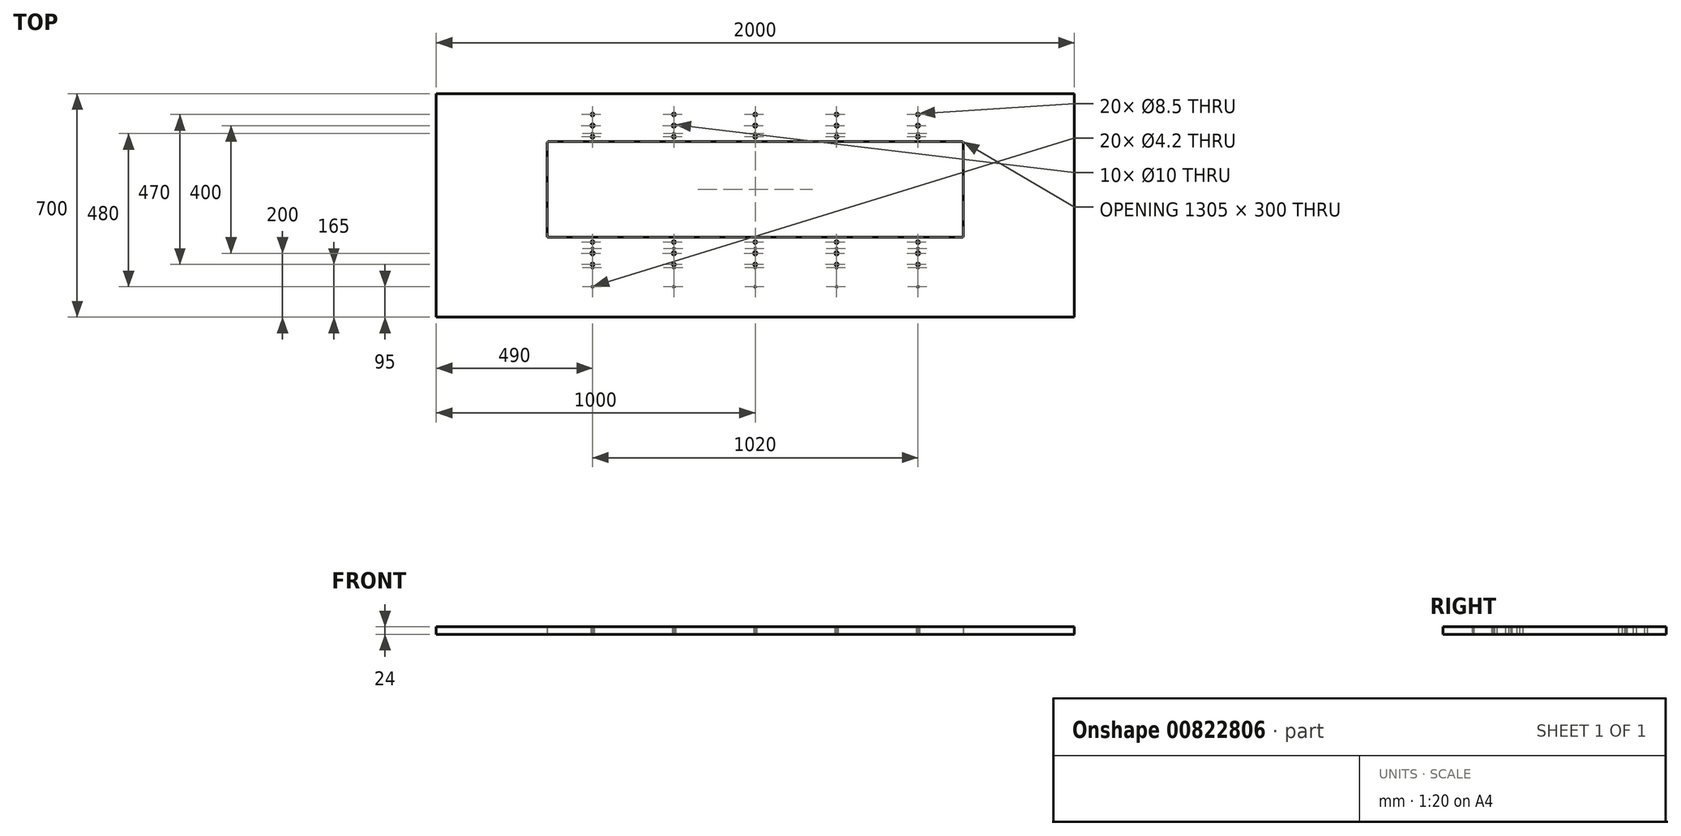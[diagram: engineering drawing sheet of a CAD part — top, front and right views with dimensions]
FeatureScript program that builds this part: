
annotation { "Feature Type Name" : "Feature", "Feature Type Description" : "" }
export const myFeature = defineFeature(function(context is Context, id is Id, definition is map)
    precondition{}
    {
        {
            var Q0;
            Q0=qCreatedBy(makeId("Top.planeOp"),FACE);
            var sketch = newSketch(context, id + "F0", { "sketchPlane" : qUnion([Q0])});
            skLineSegment(sketch, "E0.bottom", {"start": v(-652.5, -150) * mm, "end": v(652.5, -150) * mm});
            skLineSegment(sketch, "E0.top", {"start": v(-652.5, 150) * mm, "end": v(652.5, 150) * mm});
            skLineSegment(sketch, "E0.left", {"start": v(-652.5, -150) * mm, "end": v(-652.5, 150) * mm});
            skLineSegment(sketch, "E0.right", {"start": v(652.5, -150) * mm, "end": v(652.5, 150) * mm});
            skPoint(sketch, "E0.middle", {"position": v(0, 0) * mm});
            skLineSegment(sketch, "E1.top", {"start": v(-1000, 300) * mm, "end": v(1000, 300) * mm});
            skLineSegment(sketch, "E2.bottom", {"start": v(-510, 165) * mm, "end": v(510, 165) * mm, "construction": true});
            skLineSegment(sketch, "E2.top", {"start": v(-510, -165) * mm, "end": v(510, -165) * mm, "construction": true});
            skLineSegment(sketch, "E2.left", {"start": v(-510, 165) * mm, "end": v(-510, -165) * mm, "construction": true});
            skLineSegment(sketch, "E2.right", {"start": v(510, 165) * mm, "end": v(510, -165) * mm, "construction": true});
            skLineSegment(sketch, "E3", {"start": v(-255, 314.2) * mm, "end": v(-255, -334.02) * mm, "construction": true});
            skLineSegment(sketch, "E4", {"start": v(0, 0) * mm, "end": v(0, 282.14) * mm, "construction": true});
            skLineSegment(sketch, "E5", {"start": v(0, 0) * mm, "end": v(-747.83, 0) * mm, "construction": true});
            skLineSegment(sketch, "E6.0", {"start": v(-510, 235) * mm, "end": v(510, 235) * mm, "construction": true});
            skLineSegment(sketch, "E7.0", {"start": v(-510, -235) * mm, "end": v(510, -235) * mm, "construction": true});
            skLineSegment(sketch, "E8.0", {"start": v(-510, 200) * mm, "end": v(510, 200) * mm, "construction": true});
            skCircle(sketch, "E9", {"center": v(-510, 165) * mm, "radius": 4.25 * mm});
            skCircle(sketch, "E10", {"center": v(-510, 200) * mm, "radius": 5 * mm});
            skCircle(sketch, "E11", {"center": v(-510, 235) * mm, "radius": 4.25 * mm});
            skCircle(sketch, "E12", {"center": v(-255, 165) * mm, "radius": 4.25 * mm});
            skCircle(sketch, "E13", {"center": v(-255, 200) * mm, "radius": 5 * mm});
            skCircle(sketch, "E14", {"center": v(-255, 235) * mm, "radius": 4.25 * mm});
            skCircle(sketch, "E15", {"center": v(0, 165) * mm, "radius": 4.25 * mm});
            skCircle(sketch, "E16", {"center": v(0, 200) * mm, "radius": 5 * mm});
            skCircle(sketch, "E17", {"center": v(0, 235) * mm, "radius": 4.25 * mm});
            skCircle(sketch, "E18.MirrorC", {"center": v(510, 165) * mm, "radius": 4.25 * mm});
            skCircle(sketch, "E19.MirrorC", {"center": v(510, 200) * mm, "radius": 5 * mm});
            skCircle(sketch, "E20.MirrorC", {"center": v(510, 235) * mm, "radius": 4.25 * mm});
            skCircle(sketch, "E21.MirrorC", {"center": v(255, 200) * mm, "radius": 5 * mm});
            skCircle(sketch, "E22.MirrorC", {"center": v(255, 235) * mm, "radius": 4.25 * mm});
            skCircle(sketch, "E23.MirrorC", {"center": v(255, 165) * mm, "radius": 4.25 * mm});
            skCircle(sketch, "E24.MirrorC", {"center": v(510, -165) * mm, "radius": 4.25 * mm});
            skCircle(sketch, "E25.MirrorC", {"center": v(510, -235) * mm, "radius": 4.25 * mm});
            skCircle(sketch, "E26.MirrorC", {"center": v(510, -200) * mm, "radius": 5 * mm});
            skCircle(sketch, "E27.MirrorC", {"center": v(-510, -235) * mm, "radius": 4.25 * mm});
            skCircle(sketch, "E28.MirrorC", {"center": v(-510, -165) * mm, "radius": 4.25 * mm});
            skCircle(sketch, "E29.MirrorC", {"center": v(-510, -200) * mm, "radius": 5 * mm});
            skCircle(sketch, "E30.MirrorC", {"center": v(0, -200) * mm, "radius": 5 * mm});
            skCircle(sketch, "E31.MirrorC", {"center": v(0, -165) * mm, "radius": 4.25 * mm});
            skCircle(sketch, "E32.MirrorC", {"center": v(0, -235) * mm, "radius": 4.25 * mm});
            skCircle(sketch, "E33.MirrorC", {"center": v(-255, -200) * mm, "radius": 5 * mm});
            skCircle(sketch, "E34.MirrorC", {"center": v(255, -235) * mm, "radius": 4.25 * mm});
            skCircle(sketch, "E35.MirrorC", {"center": v(-255, -235) * mm, "radius": 4.25 * mm});
            skCircle(sketch, "E36.MirrorC", {"center": v(-255, -165) * mm, "radius": 4.25 * mm});
            skCircle(sketch, "E37.MirrorC", {"center": v(255, -200) * mm, "radius": 5 * mm});
            skCircle(sketch, "E38.MirrorC", {"center": v(255, -165) * mm, "radius": 4.25 * mm});
            skLineSegment(sketch, "E39", {"start": v(-1000, 300) * mm, "end": v(-1000, -400) * mm});
            skLineSegment(sketch, "E40", {"start": v(-1000, -400) * mm, "end": v(1000, -400) * mm});
            skLineSegment(sketch, "E41", {"start": v(1000, -400) * mm, "end": v(1000, 300) * mm});
            skSolve(sketch);
        }
        {
            var Q0;
            Q0=makeQuery(id+"F0.imprint","IMPRINT",FACE,{"disambiguationData":[TD([[makeQuery(id+"F0.imprint","IMPRINT",EDGE,{"derivedFrom":sQuery(id+"F0.wireOp",EDGE,"E0.bottom")}),-1.0]])]});
            extrude(context, id + "F1", {"entities" : qUnion([Q0]), "depth" : 24 * mm, "offsetDistance" : 25 * mm});
        }
        {
            var Q0;
            Q0=makeQuery(id+"F1.opExtrude","SWEPT_EDGE",EDGE,{"disambiguationData":[OSD([sQuery(id+"F0.wireOp",EDGE,"E0.top"),sQuery(id+"F0.wireOp",EDGE,"E0.left")])]});
            var Q1;
            Q1=makeQuery(id+"F1.opExtrude","SWEPT_EDGE",EDGE,{"disambiguationData":[OSD([sQuery(id+"F0.wireOp",EDGE,"E0.top"),sQuery(id+"F0.wireOp",EDGE,"E0.right")])]});
            var Q2;
            Q2=makeQuery(id+"F1.opExtrude","SWEPT_EDGE",EDGE,{"disambiguationData":[OSD([sQuery(id+"F0.wireOp",EDGE,"E0.bottom"),sQuery(id+"F0.wireOp",EDGE,"E0.right")])]});
            var Q3;
            Q3=makeQuery(id+"F1.opExtrude","SWEPT_EDGE",EDGE,{"disambiguationData":[OSD([sQuery(id+"F0.wireOp",EDGE,"E0.bottom"),sQuery(id+"F0.wireOp",EDGE,"E0.left")])]});
            fillet(context, id + "F2", {"entities" : qUnion([Q0, Q1, Q2, Q3]), "radius" : 5 * mm, "tangentPropagation" : true, "allowEdgeOverflow" : false});
        }
        {
            var Q0;
            Q0=makeQuery(id+"F1.opExtrude","CAP_FACE",FACE,{"disambiguationData":[OSD([sQuery(id+"F0.wireOp",EDGE,"E0.bottom"),sQuery(id+"F0.wireOp",EDGE,"E0.top"),sQuery(id+"F0.wireOp",EDGE,"E0.left"),sQuery(id+"F0.wireOp",EDGE,"E0.right"),sQuery(id+"F0.wireOp",EDGE,"E1.bottom"),sQuery(id+"F0.wireOp",EDGE,"E1.top"),sQuery(id+"F0.wireOp",EDGE,"E1.left"),sQuery(id+"F0.wireOp",EDGE,"E1.right"),sQuery(id+"F0.wireOp",EDGE,"E9"),sQuery(id+"F0.wireOp",EDGE,"E10"),sQuery(id+"F0.wireOp",EDGE,"E11"),sQuery(id+"F0.wireOp",EDGE,"E12"),sQuery(id+"F0.wireOp",EDGE,"E13"),sQuery(id+"F0.wireOp",EDGE,"E14"),sQuery(id+"F0.wireOp",EDGE,"E15"),sQuery(id+"F0.wireOp",EDGE,"E16"),sQuery(id+"F0.wireOp",EDGE,"E17"),sQuery(id+"F0.wireOp",EDGE,"E18.MirrorC"),sQuery(id+"F0.wireOp",EDGE,"E19.MirrorC"),sQuery(id+"F0.wireOp",EDGE,"E20.MirrorC"),sQuery(id+"F0.wireOp",EDGE,"E21.MirrorC"),sQuery(id+"F0.wireOp",EDGE,"E22.MirrorC"),sQuery(id+"F0.wireOp",EDGE,"E23.MirrorC"),sQuery(id+"F0.wireOp",EDGE,"E24.MirrorC"),sQuery(id+"F0.wireOp",EDGE,"E25.MirrorC"),sQuery(id+"F0.wireOp",EDGE,"E26.MirrorC"),sQuery(id+"F0.wireOp",EDGE,"E27.MirrorC"),sQuery(id+"F0.wireOp",EDGE,"E28.MirrorC"),sQuery(id+"F0.wireOp",EDGE,"E29.MirrorC"),sQuery(id+"F0.wireOp",EDGE,"E30.MirrorC"),sQuery(id+"F0.wireOp",EDGE,"E31.MirrorC"),sQuery(id+"F0.wireOp",EDGE,"E32.MirrorC"),sQuery(id+"F0.wireOp",EDGE,"E33.MirrorC"),sQuery(id+"F0.wireOp",EDGE,"E34.MirrorC"),sQuery(id+"F0.wireOp",EDGE,"E35.MirrorC"),sQuery(id+"F0.wireOp",EDGE,"E36.MirrorC"),sQuery(id+"F0.wireOp",EDGE,"E37.MirrorC"),sQuery(id+"F0.wireOp",EDGE,"E38.MirrorC")])],"isStart":false});
            var sketch = newSketch(context, id + "F3", { "sketchPlane" : qUnion([Q0])});
            skCircle(sketch, "E42.0", {"center": v(-510, 235) * mm, "radius": 4.25 * mm, "construction": true});
            skCircle(sketch, "E43.0", {"center": v(-255, 235) * mm, "radius": 4.25 * mm, "construction": true});
            skCircle(sketch, "E44.0", {"center": v(0, 235) * mm, "radius": 4.25 * mm, "construction": true});
            skLineSegment(sketch, "E45", {"start": v(0, 0) * mm, "end": v(0, 235) * mm, "construction": true});
            skLineSegment(sketch, "E46", {"start": v(0, 0) * mm, "end": v(-510, 0) * mm, "construction": true});
            skLineSegment(sketch, "E47", {"start": v(-510, 0) * mm, "end": v(-510, 235) * mm, "construction": true});
            skLineSegment(sketch, "E48", {"start": v(-255, 235) * mm, "end": v(-255, 0) * mm, "construction": true});
            skCircle(sketch, "E49.0", {"center": v(-510, -235) * mm, "radius": 4.25 * mm, "construction": true});
            skCircle(sketch, "E50.0", {"center": v(-255, -235) * mm, "radius": 4.25 * mm, "construction": true});
            skCircle(sketch, "E51.0", {"center": v(0, -235) * mm, "radius": 4.25 * mm, "construction": true});
            skLineSegment(sketch, "E52", {"start": v(-510, 0) * mm, "end": v(-510, -235) * mm, "construction": true});
            skLineSegment(sketch, "E53", {"start": v(-255, -235) * mm, "end": v(-255, 0) * mm, "construction": true});
            skLineSegment(sketch, "E54", {"start": v(0, -235) * mm, "end": v(0, 0) * mm, "construction": true});
            skLineSegment(sketch, "E55.0", {"start": v(-647.5, 150) * mm, "end": v(647.5, 150) * mm, "construction": true});
            skLineSegment(sketch, "E56.0", {"start": v(-647.5, -150) * mm, "end": v(647.5, -150) * mm, "construction": true});
            skLineSegment(sketch, "E57", {"start": v(-602.6, -185) * mm, "end": v(29.57, -185) * mm, "construction": true});
            skLineSegment(sketch, "E58", {"start": v(29.57, -185) * mm, "end": v(29.57, -245) * mm, "construction": true});
            skLineSegment(sketch, "E59", {"start": v(29.57, -245) * mm, "end": v(-618.47, -245) * mm, "construction": true});
            skLineSegment(sketch, "E60", {"start": v(-618.47, -245) * mm, "end": v(-618.47, 175) * mm, "construction": true});
            skLineSegment(sketch, "E61", {"start": v(-618.47, 175) * mm, "end": v(51.1, 175) * mm, "construction": true});
            skCircle(sketch, "E62", {"center": v(-510, 175) * mm, "radius": 2.1 * mm});
            skCircle(sketch, "E63", {"center": v(-255, 175) * mm, "radius": 2.1 * mm});
            skCircle(sketch, "E64", {"center": v(0, 175) * mm, "radius": 2.1 * mm});
            skCircle(sketch, "E65", {"center": v(0, -185) * mm, "radius": 2.1 * mm});
            skCircle(sketch, "E66", {"center": v(-255, -185) * mm, "radius": 2.1 * mm});
            skCircle(sketch, "E67", {"center": v(-510, -185) * mm, "radius": 2.1 * mm});
            skLineSegment(sketch, "E68", {"start": v(-510, -235) * mm, "end": v(-510, -342.58) * mm, "construction": true});
            skLineSegment(sketch, "E69", {"start": v(-255, -235) * mm, "end": v(-255, -344.4) * mm, "construction": true});
            skLineSegment(sketch, "E70", {"start": v(0, -235) * mm, "end": v(0, -337.73) * mm, "construction": true});
            skCircle(sketch, "E71", {"center": v(0, -245) * mm, "radius": 2.1 * mm});
            skCircle(sketch, "E72", {"center": v(-255, -245) * mm, "radius": 2.1 * mm});
            skCircle(sketch, "E73", {"center": v(-510, -245) * mm, "radius": 2.1 * mm});
            skCircle(sketch, "E74.MirrorC", {"center": v(255, -245) * mm, "radius": 2.1 * mm});
            skCircle(sketch, "E75.MirrorC", {"center": v(510, -245) * mm, "radius": 2.1 * mm});
            skCircle(sketch, "E76.MirrorC", {"center": v(255, -235) * mm, "radius": 4.25 * mm, "construction": true});
            skCircle(sketch, "E77.MirrorC", {"center": v(510, -235) * mm, "radius": 4.25 * mm, "construction": true});
            skCircle(sketch, "E78.MirrorC", {"center": v(255, -185) * mm, "radius": 2.1 * mm});
            skCircle(sketch, "E79.MirrorC", {"center": v(510, -185) * mm, "radius": 2.1 * mm});
            skCircle(sketch, "E80.MirrorC", {"center": v(255, 175) * mm, "radius": 2.1 * mm});
            skCircle(sketch, "E81.MirrorC", {"center": v(510, 175) * mm, "radius": 2.1 * mm});
            skLineSegment(sketch, "E82.0", {"start": v(29.57, -305) * mm, "end": v(-618.47, -305) * mm, "construction": true});
            skCircle(sketch, "E83", {"center": v(-510, -305) * mm, "radius": 2.1 * mm});
            skCircle(sketch, "E84", {"center": v(-255, -305) * mm, "radius": 2.1 * mm});
            skCircle(sketch, "E85", {"center": v(0, -305) * mm, "radius": 2.1 * mm});
            skCircle(sketch, "E86.MirrorC", {"center": v(510, -305) * mm, "radius": 2.1 * mm});
            skCircle(sketch, "E87.MirrorC", {"center": v(255, -305) * mm, "radius": 2.1 * mm});
            skSolve(sketch);
        }
        {
            var Q0;
            Q0 = qSketchRegion(id + "F3", true);
            extrude(context, id + "F4", {"entities" : qUnion([Q0]), "operationType" : NewBodyOperationType.REMOVE, "oppositeDirection" : true, "depth" : 20 * mm, "offsetDistance" : 25 * mm});
        }
        {
            var Q0;
            Q0=makeQuery(id+"F4.boolean.opBoolean","COPY",FACE,{"derivedFrom":makeQuery(id+"F4.opExtrude","CAP_FACE",FACE,{"disambiguationData":[OSD([sQuery(id+"F3.wireOp",EDGE,"E62")])],"isStart":false})});
            var Q1;
            Q1=makeQuery(id+"F4.boolean.opBoolean","COPY",FACE,{"derivedFrom":makeQuery(id+"F4.opExtrude","CAP_FACE",FACE,{"disambiguationData":[OSD([sQuery(id+"F3.wireOp",EDGE,"E63")])],"isStart":false})});
            var Q2;
            Q2=makeQuery(id+"F4.boolean.opBoolean","COPY",FACE,{"derivedFrom":makeQuery(id+"F4.opExtrude","CAP_FACE",FACE,{"disambiguationData":[OSD([sQuery(id+"F3.wireOp",EDGE,"E64")])],"isStart":false})});
            var Q3;
            Q3=makeQuery(id+"F4.boolean.opBoolean","COPY",FACE,{"derivedFrom":makeQuery(id+"F4.opExtrude","CAP_FACE",FACE,{"disambiguationData":[OSD([sQuery(id+"F3.wireOp",EDGE,"E80.MirrorC")])],"isStart":false})});
            var Q4;
            Q4=makeQuery(id+"F4.boolean.opBoolean","COPY",FACE,{"derivedFrom":makeQuery(id+"F4.opExtrude","CAP_FACE",FACE,{"disambiguationData":[OSD([sQuery(id+"F3.wireOp",EDGE,"E81.MirrorC")])],"isStart":false})});
            var Q5;
            Q5=makeQuery(id+"F4.boolean.opBoolean","COPY",FACE,{"derivedFrom":makeQuery(id+"F4.opExtrude","CAP_FACE",FACE,{"disambiguationData":[OSD([sQuery(id+"F3.wireOp",EDGE,"E79.MirrorC")])],"isStart":false})});
            var Q6;
            Q6=makeQuery(id+"F4.boolean.opBoolean","COPY",FACE,{"derivedFrom":makeQuery(id+"F4.opExtrude","CAP_FACE",FACE,{"disambiguationData":[OSD([sQuery(id+"F3.wireOp",EDGE,"E75.MirrorC")])],"isStart":false})});
            var Q7;
            Q7=makeQuery(id+"F4.boolean.opBoolean","COPY",FACE,{"derivedFrom":makeQuery(id+"F4.opExtrude","CAP_FACE",FACE,{"disambiguationData":[OSD([sQuery(id+"F3.wireOp",EDGE,"E74.MirrorC")])],"isStart":false})});
            var Q8;
            Q8=makeQuery(id+"F4.boolean.opBoolean","COPY",FACE,{"derivedFrom":makeQuery(id+"F4.opExtrude","CAP_FACE",FACE,{"disambiguationData":[OSD([sQuery(id+"F3.wireOp",EDGE,"E78.MirrorC")])],"isStart":false})});
            var Q9;
            Q9=makeQuery(id+"F4.boolean.opBoolean","COPY",FACE,{"derivedFrom":makeQuery(id+"F4.opExtrude","CAP_FACE",FACE,{"disambiguationData":[OSD([sQuery(id+"F3.wireOp",EDGE,"E71")])],"isStart":false})});
            var Q10;
            Q10=makeQuery(id+"F4.boolean.opBoolean","COPY",FACE,{"derivedFrom":makeQuery(id+"F4.opExtrude","CAP_FACE",FACE,{"disambiguationData":[OSD([sQuery(id+"F3.wireOp",EDGE,"E65")])],"isStart":false})});
            var Q11;
            Q11=makeQuery(id+"F4.boolean.opBoolean","COPY",FACE,{"derivedFrom":makeQuery(id+"F4.opExtrude","CAP_FACE",FACE,{"disambiguationData":[OSD([sQuery(id+"F3.wireOp",EDGE,"E72")])],"isStart":false})});
            var Q12;
            Q12=makeQuery(id+"F4.boolean.opBoolean","COPY",FACE,{"derivedFrom":makeQuery(id+"F4.opExtrude","CAP_FACE",FACE,{"disambiguationData":[OSD([sQuery(id+"F3.wireOp",EDGE,"E66")])],"isStart":false})});
            var Q13;
            Q13=makeQuery(id+"F4.boolean.opBoolean","COPY",FACE,{"derivedFrom":makeQuery(id+"F4.opExtrude","CAP_FACE",FACE,{"disambiguationData":[OSD([sQuery(id+"F3.wireOp",EDGE,"E67")])],"isStart":false})});
            var Q14;
            Q14=makeQuery(id+"F4.boolean.opBoolean","COPY",FACE,{"derivedFrom":makeQuery(id+"F4.opExtrude","CAP_FACE",FACE,{"disambiguationData":[OSD([sQuery(id+"F3.wireOp",EDGE,"E73")])],"isStart":false})});
            var Q15;
            Q15=makeQuery(id+"F4.boolean.opBoolean","COPY",FACE,{"derivedFrom":makeQuery(id+"F4.opExtrude","CAP_FACE",FACE,{"disambiguationData":[OSD([sQuery(id+"F3.wireOp",EDGE,"E83")])],"isStart":false})});
            var Q16;
            Q16=makeQuery(id+"F4.boolean.opBoolean","COPY",FACE,{"derivedFrom":makeQuery(id+"F4.opExtrude","CAP_FACE",FACE,{"disambiguationData":[OSD([sQuery(id+"F3.wireOp",EDGE,"E84")])],"isStart":false})});
            var Q17;
            Q17=makeQuery(id+"F4.boolean.opBoolean","COPY",FACE,{"derivedFrom":makeQuery(id+"F4.opExtrude","CAP_FACE",FACE,{"disambiguationData":[OSD([sQuery(id+"F3.wireOp",EDGE,"E85")])],"isStart":false})});
            var Q18;
            Q18=makeQuery(id+"F4.boolean.opBoolean","COPY",FACE,{"derivedFrom":makeQuery(id+"F4.opExtrude","CAP_FACE",FACE,{"disambiguationData":[OSD([sQuery(id+"F3.wireOp",EDGE,"E87.MirrorC")])],"isStart":false})});
            var Q19;
            Q19=makeQuery(id+"F4.boolean.opBoolean","COPY",FACE,{"derivedFrom":makeQuery(id+"F4.opExtrude","CAP_FACE",FACE,{"disambiguationData":[OSD([sQuery(id+"F3.wireOp",EDGE,"E86.MirrorC")])],"isStart":false})});
            chamfer(context, id + "F5", {"entities" : qUnion([Q0, Q1, Q2, Q3, Q4, Q5, Q6, Q7, Q8, Q9, Q10, Q11, Q12, Q13, Q14, Q15, Q16, Q17, Q18, Q19]), "width" : 2.1 * mm, "tangentPropagation" : true});
        }
        {
            var Q0;
            Q0=makeQuery(id+"F1.opExtrude","SWEPT_FACE",FACE,{"disambiguationData":[OSD([sQuery(id+"F0.wireOp",EDGE,"E11")])]});
            var Q1;
            Q1=makeQuery(id+"F1.opExtrude","SWEPT_FACE",FACE,{"disambiguationData":[OSD([sQuery(id+"F0.wireOp",EDGE,"E10")])]});
            var Q2;
            Q2=makeQuery(id+"F1.opExtrude","SWEPT_FACE",FACE,{"disambiguationData":[OSD([sQuery(id+"F0.wireOp",EDGE,"E9")])]});
            var Q3;
            Q3=makeQuery(id+"F4.boolean.opBoolean","COPY",EDGE,{"derivedFrom":makeQuery(id+"F4.opExtrude","CAP_EDGE",EDGE,{"disambiguationData":[OSD([sQuery(id+"F3.wireOp",EDGE,"E62")])],"isStart":true})});
            var Q4;
            Q4=makeQuery(id+"F1.opExtrude","SWEPT_FACE",FACE,{"disambiguationData":[OSD([sQuery(id+"F0.wireOp",EDGE,"E14")])]});
            var Q5;
            Q5=makeQuery(id+"F1.opExtrude","SWEPT_FACE",FACE,{"disambiguationData":[OSD([sQuery(id+"F0.wireOp",EDGE,"E13")])]});
            var Q6;
            Q6=makeQuery(id+"F1.opExtrude","SWEPT_FACE",FACE,{"disambiguationData":[OSD([sQuery(id+"F0.wireOp",EDGE,"E12")])]});
            var Q7;
            Q7=makeQuery(id+"F4.boolean.opBoolean","COPY",EDGE,{"derivedFrom":makeQuery(id+"F4.opExtrude","CAP_EDGE",EDGE,{"disambiguationData":[OSD([sQuery(id+"F3.wireOp",EDGE,"E63")])],"isStart":true})});
            var Q8;
            Q8=makeQuery(id+"F1.opExtrude","SWEPT_FACE",FACE,{"disambiguationData":[OSD([sQuery(id+"F0.wireOp",EDGE,"E17")])]});
            var Q9;
            Q9=makeQuery(id+"F1.opExtrude","SWEPT_FACE",FACE,{"disambiguationData":[OSD([sQuery(id+"F0.wireOp",EDGE,"E16")])]});
            var Q10;
            Q10=makeQuery(id+"F1.opExtrude","SWEPT_FACE",FACE,{"disambiguationData":[OSD([sQuery(id+"F0.wireOp",EDGE,"E15")])]});
            var Q11;
            Q11=makeQuery(id+"F4.boolean.opBoolean","COPY",EDGE,{"derivedFrom":makeQuery(id+"F4.opExtrude","CAP_EDGE",EDGE,{"disambiguationData":[OSD([sQuery(id+"F3.wireOp",EDGE,"E64")])],"isStart":true})});
            var Q12;
            Q12=makeQuery(id+"F1.opExtrude","SWEPT_FACE",FACE,{"disambiguationData":[OSD([sQuery(id+"F0.wireOp",EDGE,"E22.MirrorC")])]});
            var Q13;
            Q13=makeQuery(id+"F1.opExtrude","SWEPT_FACE",FACE,{"disambiguationData":[OSD([sQuery(id+"F0.wireOp",EDGE,"E21.MirrorC")])]});
            var Q14;
            Q14=makeQuery(id+"F1.opExtrude","SWEPT_FACE",FACE,{"disambiguationData":[OSD([sQuery(id+"F0.wireOp",EDGE,"E23.MirrorC")])]});
            var Q15;
            Q15=makeQuery(id+"F4.boolean.opBoolean","COPY",EDGE,{"derivedFrom":makeQuery(id+"F4.opExtrude","CAP_EDGE",EDGE,{"disambiguationData":[OSD([sQuery(id+"F3.wireOp",EDGE,"E80.MirrorC")])],"isStart":true})});
            var Q16;
            Q16=makeQuery(id+"F1.opExtrude","SWEPT_FACE",FACE,{"disambiguationData":[OSD([sQuery(id+"F0.wireOp",EDGE,"E20.MirrorC")])]});
            var Q17;
            Q17=makeQuery(id+"F1.opExtrude","SWEPT_FACE",FACE,{"disambiguationData":[OSD([sQuery(id+"F0.wireOp",EDGE,"E19.MirrorC")])]});
            var Q18;
            Q18=makeQuery(id+"F1.opExtrude","SWEPT_FACE",FACE,{"disambiguationData":[OSD([sQuery(id+"F0.wireOp",EDGE,"E18.MirrorC")])]});
            var Q19;
            Q19=makeQuery(id+"F4.boolean.opBoolean","COPY",EDGE,{"derivedFrom":makeQuery(id+"F4.opExtrude","CAP_EDGE",EDGE,{"disambiguationData":[OSD([sQuery(id+"F3.wireOp",EDGE,"E81.MirrorC")])],"isStart":true})});
            var Q20;
            Q20=makeQuery(id+"F1.opExtrude","SWEPT_FACE",FACE,{"disambiguationData":[OSD([sQuery(id+"F0.wireOp",EDGE,"E24.MirrorC")])]});
            var Q21;
            Q21=makeQuery(id+"F4.boolean.opBoolean","COPY",EDGE,{"derivedFrom":makeQuery(id+"F4.opExtrude","CAP_EDGE",EDGE,{"disambiguationData":[OSD([sQuery(id+"F3.wireOp",EDGE,"E79.MirrorC")])],"isStart":true})});
            var Q22;
            Q22=makeQuery(id+"F1.opExtrude","SWEPT_FACE",FACE,{"disambiguationData":[OSD([sQuery(id+"F0.wireOp",EDGE,"E26.MirrorC")])]});
            var Q23;
            Q23=makeQuery(id+"F4.boolean.opBoolean","COPY",EDGE,{"derivedFrom":makeQuery(id+"F4.opExtrude","CAP_EDGE",EDGE,{"disambiguationData":[OSD([sQuery(id+"F3.wireOp",EDGE,"E75.MirrorC")])],"isStart":true})});
            var Q24;
            Q24=makeQuery(id+"F1.opExtrude","SWEPT_FACE",FACE,{"disambiguationData":[OSD([sQuery(id+"F0.wireOp",EDGE,"E25.MirrorC")])]});
            var Q25;
            Q25=makeQuery(id+"F4.boolean.opBoolean","COPY",EDGE,{"derivedFrom":makeQuery(id+"F4.opExtrude","CAP_EDGE",EDGE,{"disambiguationData":[OSD([sQuery(id+"F3.wireOp",EDGE,"E74.MirrorC")])],"isStart":true})});
            var Q26;
            Q26=makeQuery(id+"F4.boolean.opBoolean","COPY",EDGE,{"derivedFrom":makeQuery(id+"F4.opExtrude","CAP_EDGE",EDGE,{"disambiguationData":[OSD([sQuery(id+"F3.wireOp",EDGE,"E78.MirrorC")])],"isStart":true})});
            var Q27;
            Q27=makeQuery(id+"F1.opExtrude","SWEPT_FACE",FACE,{"disambiguationData":[OSD([sQuery(id+"F0.wireOp",EDGE,"E38.MirrorC")])]});
            var Q28;
            Q28=makeQuery(id+"F1.opExtrude","SWEPT_FACE",FACE,{"disambiguationData":[OSD([sQuery(id+"F0.wireOp",EDGE,"E37.MirrorC")])]});
            var Q29;
            Q29=makeQuery(id+"F1.opExtrude","SWEPT_FACE",FACE,{"disambiguationData":[OSD([sQuery(id+"F0.wireOp",EDGE,"E34.MirrorC")])]});
            var Q30;
            Q30=makeQuery(id+"F4.boolean.opBoolean","COPY",EDGE,{"derivedFrom":makeQuery(id+"F4.opExtrude","CAP_EDGE",EDGE,{"disambiguationData":[OSD([sQuery(id+"F3.wireOp",EDGE,"E65")])],"isStart":true})});
            var Q31;
            Q31=makeQuery(id+"F1.opExtrude","SWEPT_FACE",FACE,{"disambiguationData":[OSD([sQuery(id+"F0.wireOp",EDGE,"E31.MirrorC")])]});
            var Q32;
            Q32=makeQuery(id+"F1.opExtrude","SWEPT_FACE",FACE,{"disambiguationData":[OSD([sQuery(id+"F0.wireOp",EDGE,"E30.MirrorC")])]});
            var Q33;
            Q33=makeQuery(id+"F1.opExtrude","SWEPT_FACE",FACE,{"disambiguationData":[OSD([sQuery(id+"F0.wireOp",EDGE,"E32.MirrorC")])]});
            var Q34;
            Q34=makeQuery(id+"F4.boolean.opBoolean","COPY",EDGE,{"derivedFrom":makeQuery(id+"F4.opExtrude","CAP_EDGE",EDGE,{"disambiguationData":[OSD([sQuery(id+"F3.wireOp",EDGE,"E71")])],"isStart":true})});
            var Q35;
            Q35=makeQuery(id+"F1.opExtrude","SWEPT_FACE",FACE,{"disambiguationData":[OSD([sQuery(id+"F0.wireOp",EDGE,"E35.MirrorC")])]});
            var Q36;
            Q36=makeQuery(id+"F1.opExtrude","SWEPT_FACE",FACE,{"disambiguationData":[OSD([sQuery(id+"F0.wireOp",EDGE,"E33.MirrorC")])]});
            var Q37;
            Q37=makeQuery(id+"F1.opExtrude","SWEPT_FACE",FACE,{"disambiguationData":[OSD([sQuery(id+"F0.wireOp",EDGE,"E36.MirrorC")])]});
            var Q38;
            Q38=makeQuery(id+"F4.boolean.opBoolean","COPY",EDGE,{"derivedFrom":makeQuery(id+"F4.opExtrude","CAP_EDGE",EDGE,{"disambiguationData":[OSD([sQuery(id+"F3.wireOp",EDGE,"E66")])],"isStart":true})});
            var Q39;
            Q39=makeQuery(id+"F4.boolean.opBoolean","COPY",EDGE,{"derivedFrom":makeQuery(id+"F4.opExtrude","CAP_EDGE",EDGE,{"disambiguationData":[OSD([sQuery(id+"F3.wireOp",EDGE,"E72")])],"isStart":true})});
            var Q40;
            Q40=makeQuery(id+"F1.opExtrude","SWEPT_FACE",FACE,{"disambiguationData":[OSD([sQuery(id+"F0.wireOp",EDGE,"E27.MirrorC")])]});
            var Q41;
            Q41=makeQuery(id+"F1.opExtrude","SWEPT_FACE",FACE,{"disambiguationData":[OSD([sQuery(id+"F0.wireOp",EDGE,"E29.MirrorC")])]});
            var Q42;
            Q42=makeQuery(id+"F1.opExtrude","SWEPT_FACE",FACE,{"disambiguationData":[OSD([sQuery(id+"F0.wireOp",EDGE,"E28.MirrorC")])]});
            var Q43;
            Q43=makeQuery(id+"F4.boolean.opBoolean","COPY",EDGE,{"derivedFrom":makeQuery(id+"F4.opExtrude","CAP_EDGE",EDGE,{"disambiguationData":[OSD([sQuery(id+"F3.wireOp",EDGE,"E67")])],"isStart":true})});
            var Q44;
            Q44=makeQuery(id+"F4.boolean.opBoolean","COPY",EDGE,{"derivedFrom":makeQuery(id+"F4.opExtrude","CAP_EDGE",EDGE,{"disambiguationData":[OSD([sQuery(id+"F3.wireOp",EDGE,"E73")])],"isStart":true})});
            chamfer(context, id + "F6", {"entities" : qUnion([Q0, Q1, Q2, Q3, Q4, Q5, Q6, Q7, Q8, Q9, Q10, Q11, Q12, Q13, Q14, Q15, Q16, Q17, Q18, Q19, Q20, Q21, Q22, Q23, Q24, Q25, Q26, Q27, Q28, Q29, Q30, Q31, Q32, Q33, Q34, Q35, Q36, Q37, Q38, Q39, Q40, Q41, Q42, Q43, Q44]), "width" : 0.5 * mm, "tangentPropagation" : true});
        }
    });
